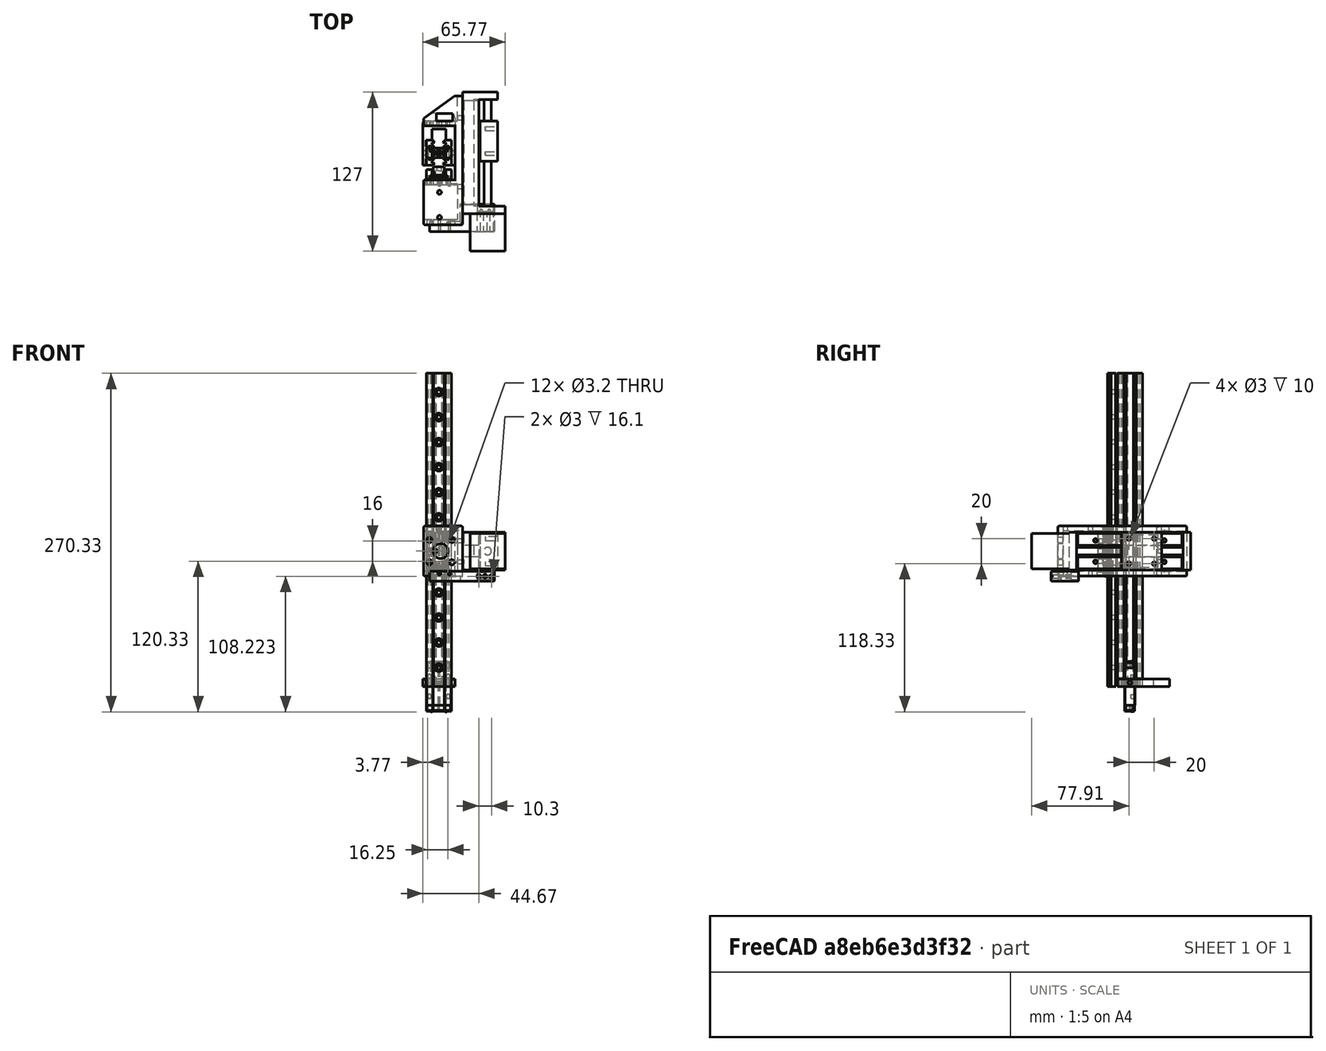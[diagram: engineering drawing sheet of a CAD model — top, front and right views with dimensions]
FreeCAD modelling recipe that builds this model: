
FCSTD DOCUMENT  (FreeCAD 1.0R39109 (Git))
Label: x_carriage
License: All rights reserved
LicenseURL: https://en.wikipedia.org/wiki/All_rights_reserved
objects: Sketcher::SketchObject×32, PartDesign::Pocket×19, PartDesign::Pad×17, Part::Feature×12, PartDesign::Mirrored×5, PartDesign::Body×4, PartDesign::LinearPattern×4, PartDesign::Fillet×4, PartDesign::MultiTransform×3, App::Part×2, Part::Mirroring×2, Part::Extrusion×1, Part::Fillet×1, Mesh::Feature×1
note: 228 computed .brp shape members not serialized (recipe doc carries the construction recipe); baked Part::Feature solids carry a one-line shape summary decoded from their .brp

FEATURE [Part::Feature] Part__Feature  label="MGN9-H"
  shape: bbox 20 x 8 x 29.9 mm, 47 faces (baked)
FEATURE [Part::Feature] Part__Feature001  label="MGN9-H001"
  shape: bbox 20 x 7.7 x 4.1 mm, 23 faces (baked)
FEATURE [Part::Feature] Part__Feature002  label="MGN9-H002"
  shape: bbox 2.603 x 2.603 x 1.283 mm, 15 faces (baked)
FEATURE [Part::Feature] Part__Feature003  label="MGN9-H003"
  shape: bbox 2.603 x 2.603 x 1.283 mm, 15 faces (baked)
FEATURE [Part::Feature] Part__Feature004  label="MGN9-H004"
  shape: bbox 20 x 7.7 x 0.9 mm, 57 faces (baked)
FEATURE [Part::Feature] Part__Feature005  label="MGN9-H005"
  shape: bbox 20 x 7.7 x 4.1 mm, 23 faces (baked)
FEATURE [Part::Feature] Part__Feature006  label="MGN9-H006"
  shape: bbox 20 x 7.7 x 0.9 mm, 57 faces (baked)
FEATURE [Part::Feature] Part__Feature007  label="MGN9-H007"
  shape: bbox 2.603 x 2.603 x 1.283 mm, 15 faces (baked)
FEATURE [Part::Feature] Part__Feature008  label="MGN9-H008"
  shape: bbox 2.603 x 2.603 x 1.283 mm, 15 faces (baked)
FEATURE [App::Part] MGN9_H  label="MGN9-H009"
  Group = -> [Part__Feature,Part__Feature001,Part__Feature002,Part__Feature003,Part__Feature004,Part__Feature005,Part__Feature006,Part__Feature007,Part__Feature008]
  Origin = -> Origin001
  Placement = pos=(0,17.3,108) rot=(0,0,1;0rad)
FEATURE [Part::Feature] Part__Feature009  label="MGN9"
  Placement = pos=(0,14.5,0) rot=(0,0,1;0rad)
  shape: bbox 9 x 6.5 x 250 mm, 130 faces (baked)
FEATURE [Sketcher::SketchObject] Sketch001
  ArcFitTolerance = 0
  FullyConstrained = false
  MakeInternals = false
  sketch-geometry (49):
    g0: Circle CenterX=0 CenterY=0 CenterZ=0 NormalX=0 NormalY=0 NormalZ=-1 AngleXU=0 Radius=2.1
    g1: LineSegment StartX=-2.84 StartY=3.90066 StartZ=0 EndX=-5.49934 EndY=6.56 EndZ=0
    g2: LineSegment StartX=-5.49934 StartY=6.56 StartZ=0 EndX=-5.49934 EndY=8.2 EndZ=0
    g3: LineSegment StartX=-5.49934 StartY=8.2 StartZ=0 EndX=-3.1 EndY=8.2 EndZ=0
    g4: LineSegment StartX=-3.1 StartY=8.2 StartZ=0 EndX=-4.9 EndY=10 EndZ=0
    g5: LineSegment StartX=-4.9 StartY=10 StartZ=0 EndX=-10 EndY=10 EndZ=0
    g6: LineSegment StartX=-10 StartY=10 StartZ=0 EndX=-10 EndY=4.9 EndZ=0
    g7: LineSegment StartX=-10 StartY=4.9 StartZ=0 EndX=-8.2 EndY=3.1 EndZ=0
    g8: LineSegment StartX=-8.2 StartY=3.1 StartZ=0 EndX=-8.2 EndY=5.49934 EndZ=0
    g9: LineSegment StartX=-8.2 StartY=5.49934 StartZ=0 EndX=-6.56 EndY=5.49934 EndZ=0
    g10: LineSegment StartX=-6.56 StartY=5.49934 StartZ=0 EndX=-3.90066 EndY=2.84 EndZ=0
    g11: LineSegment StartX=-3.90066 StartY=2.84 StartZ=0 EndX=-3.90066 EndY=-1.3e-15 EndZ=0
    g12: LineSegment StartX=-3.90066 StartY=-1.1e-15 StartZ=0 EndX=-3.90066 EndY=-2.84 EndZ=0
    g13: LineSegment StartX=-3.90066 StartY=-2.84 StartZ=0 EndX=-6.56 EndY=-5.49934 EndZ=0
    g14: LineSegment StartX=-6.56 StartY=-5.49934 StartZ=0 EndX=-8.2 EndY=-5.49934 EndZ=0
    g15: LineSegment StartX=-8.2 StartY=-5.49934 StartZ=0 EndX=-8.2 EndY=-3.1 EndZ=0
    g16: LineSegment StartX=-8.2 StartY=-3.1 StartZ=0 EndX=-10 EndY=-4.9 EndZ=0
    g17: LineSegment StartX=-10 StartY=-4.9 StartZ=0 EndX=-10 EndY=-10 EndZ=0
    g18: LineSegment StartX=-10 StartY=-10 StartZ=0 EndX=-4.9 EndY=-10 EndZ=0
    g19: LineSegment StartX=-4.9 StartY=-10 StartZ=0 EndX=-3.1 EndY=-8.2 EndZ=0
    g20: LineSegment StartX=-3.1 StartY=-8.2 StartZ=0 EndX=-5.49934 EndY=-8.2 EndZ=0
    g21: LineSegment StartX=-5.49934 StartY=-8.2 StartZ=0 EndX=-5.49934 EndY=-6.56 EndZ=0
    g22: LineSegment StartX=-5.49934 StartY=-6.56 StartZ=0 EndX=-2.84 EndY=-3.90066 EndZ=0
    g23: LineSegment StartX=-2.84 StartY=-3.90066 StartZ=0 EndX=-4e-16 EndY=-3.90066 EndZ=0
    g24: LineSegment StartX=-6e-16 StartY=-3.90066 StartZ=0 EndX=2.84 EndY=-3.90066 EndZ=0
    g25: LineSegment StartX=2.84 StartY=-3.90066 StartZ=0 EndX=5.49934 EndY=-6.56 EndZ=0
    g26: LineSegment StartX=5.49934 StartY=-6.56 StartZ=0 EndX=5.49934 EndY=-8.2 EndZ=0
    g27: LineSegment StartX=5.49934 StartY=-8.2 StartZ=0 EndX=3.1 EndY=-8.2 EndZ=0
    g28: LineSegment StartX=3.1 StartY=-8.2 StartZ=0 EndX=4.9 EndY=-10 EndZ=0
    g29: LineSegment StartX=4.9 StartY=-10 StartZ=0 EndX=10 EndY=-10 EndZ=0
    g30: LineSegment StartX=10 StartY=-10 StartZ=0 EndX=10 EndY=-4.9 EndZ=0
    g31: LineSegment StartX=10 StartY=-4.9 StartZ=0 EndX=8.2 EndY=-3.1 EndZ=0
    g32: LineSegment StartX=8.2 StartY=-3.1 StartZ=0 EndX=8.2 EndY=-5.49934 EndZ=0
    g33: LineSegment StartX=8.2 StartY=-5.49934 StartZ=0 EndX=6.56 EndY=-5.49934 EndZ=0
    g34: LineSegment StartX=6.56 StartY=-5.49934 StartZ=0 EndX=3.90066 EndY=-2.84 EndZ=0
    g35: LineSegment StartX=3.90066 StartY=-2.84 StartZ=0 EndX=3.90066 EndY=-1.3e-15 EndZ=0
    g36: LineSegment StartX=3.90066 StartY=-1.1e-15 StartZ=0 EndX=3.90066 EndY=2.84 EndZ=0
    g37: LineSegment StartX=3.90066 StartY=2.84 StartZ=0 EndX=6.56 EndY=5.49934 EndZ=0
    g38: LineSegment StartX=6.56 StartY=5.49934 StartZ=0 EndX=8.2 EndY=5.49934 EndZ=0
    g39: LineSegment StartX=8.2 StartY=5.49934 StartZ=0 EndX=8.2 EndY=3.1 EndZ=0
    g40: LineSegment StartX=8.2 StartY=3.1 StartZ=0 EndX=10 EndY=4.9 EndZ=0
    g41: LineSegment StartX=10 StartY=4.9 StartZ=0 EndX=10 EndY=10 EndZ=0
    g42: LineSegment StartX=10 StartY=10 StartZ=0 EndX=4.9 EndY=10 EndZ=0
    g43: LineSegment StartX=4.9 StartY=10 StartZ=0 EndX=3.1 EndY=8.2 EndZ=0
    g44: LineSegment StartX=3.1 StartY=8.2 StartZ=0 EndX=5.49934 EndY=8.2 EndZ=0
    g45: LineSegment StartX=5.49934 StartY=8.2 StartZ=0 EndX=5.49934 EndY=6.56 EndZ=0
    g46: LineSegment StartX=5.49934 StartY=6.56 StartZ=0 EndX=2.84 EndY=3.90066 EndZ=0
    g47: LineSegment StartX=2.84 StartY=3.90066 StartZ=0 EndX=0 EndY=3.90066 EndZ=0
    g48: LineSegment StartX=0 StartY=3.90066 StartZ=0 EndX=-2.84 EndY=3.90066 EndZ=0
FEATURE [Part::Extrusion] Extrude  label="2020"
  Base = -> Sketch001
  Dir = (0,0,1)
  DirMode = 2
  FaceMakerClass = Part::FaceMakerBullseye
  FaceMakerMode = 3
  LengthFwd = 250
  LengthRev = 0
  Solid = true
  Symmetric = false
FEATURE [Part::Fillet] Fillet  label="2020 V-slot"
  Base = -> Extrude
  EdgeLinks = -> Extrude [Edge14,Edge50,Edge86,Edge122]
  Edges = 4 edges r=1: [Edge14,Edge50,Edge86,Edge122]
FEATURE [Part::Mirroring] Part__Mirroring  label="MGN9-H009 (Mirror #1)"
  Base = (0,0,0)
  Normal = (0,1,0)
  Source = -> MGN9_H
FEATURE [Part::Mirroring] Part__Mirroring001  label="MGN9 (Mirror #2)"
  Base = (0,0,0)
  Normal = (0,1,0)
  Source = -> Part__Feature009
FEATURE [Sketcher::SketchObject] Sketch
  ArcFitTolerance = 1e-06
  AttachmentSupport = -> [YZ_Plane]
  FullyConstrained = true
  MakeInternals = false
  MapMode = 5
  Placement = pos=(0,0,0) rot=(0.57735,0.57735,0.57735;2.0944rad)
  sketch-geometry (5):
    g0: LineSegment StartX=-25.5 StartY=-20 StartZ=0 EndX=25.5 EndY=-20 EndZ=0
    g1: LineSegment StartX=25.5 StartY=-20 StartZ=0 EndX=25.5 EndY=20 EndZ=0
    g2: LineSegment StartX=25.5 StartY=20 StartZ=0 EndX=-25.5 EndY=20 EndZ=0
    g3: LineSegment StartX=-25.5 StartY=20 StartZ=0 EndX=-25.5 EndY=-20 EndZ=0
    g4: GeomPoint [constr] X=0 Y=0 Z=0
  constraints (12):
    c: Coincident(g0,g1)
    c: Coincident(g1,g2)
    c: Coincident(g2,g3)
    c: Coincident(g3,g0)
    c: Horizontal(g0)
    c: Horizontal(g2)
    c: Vertical(g1)
    c: Vertical(g3)
    c: Symmetric(g2,g0,g4)
    c: Distance(g1,g3) = 51
    c: Distance(g0,g2) = 40
    c: Coincident(g4,g-1)
FEATURE [PartDesign::Pad] Pad  label="carriageBase"
  Direction = (1,0,0)
  Length = 6
  Length2 = 10
  Placement = pos=(0,0,0) rot=(1,1,1;2.0944rad)
  Profile = -> Sketch
  ReferenceAxis = -> Sketch [N_Axis]
  Refine = true
  Suppressed = false
  Type = 0
FEATURE [Sketcher::SketchObject] Sketch002
  ArcFitTolerance = 1e-06
  AttachmentSupport = -> [Pad]
  ExternalGeometry = -> [Pad]
  FullyConstrained = true
  MakeInternals = false
  MapMode = 5
  Placement = pos=(0,0,0) rot=(0.57735,0.57735,-0.57735;4.18879rad)
  sketch-geometry (8):
    g0: LineSegment StartX=25.5 StartY=20 StartZ=0 EndX=21.5 EndY=20 EndZ=0
    g1: LineSegment StartX=21.5 StartY=20 StartZ=0 EndX=21.5 EndY=-20 EndZ=0
    g2: LineSegment StartX=21.5 StartY=-20 StartZ=0 EndX=25.5 EndY=-20 EndZ=0
    g3: LineSegment StartX=25.5 StartY=-20 StartZ=0 EndX=25.5 EndY=20 EndZ=0
    g4: LineSegment StartX=-25.5 StartY=20 StartZ=0 EndX=-25.5 EndY=-20 EndZ=0
    g5: LineSegment StartX=-25.5 StartY=-20 StartZ=0 EndX=-21.5 EndY=-20 EndZ=0
    g6: LineSegment StartX=-21.5 StartY=-20 StartZ=0 EndX=-21.5 EndY=20 EndZ=0
    g7: LineSegment StartX=-21.5 StartY=20 StartZ=0 EndX=-25.5 EndY=20 EndZ=0
  constraints (22):
    c: Coincident(g0,g1)
    c: Coincident(g1,g2)
    c: Coincident(g2,g3)
    c: Coincident(g3,g0)
    c: Horizontal(g0)
    c: Horizontal(g2)
    c: Vertical(g1)
    c: Vertical(g3)
    c: Distance(g1,g3) = 4
    c: Coincident(g0,g-3)
    c: PointOnObject(g1,g-4)
    c: Coincident(g4,g5)
    c: Coincident(g5,g6)
    c: Coincident(g6,g7)
    c: Coincident(g7,g4)
    c: Vertical(g4)
    c: Vertical(g6)
    c: Horizontal(g5)
    c: Horizontal(g7)
    c: Coincident(g4,g-3)
    c: PointOnObject(g5,g-4)
    c: Equal(g7,g0)
FEATURE [PartDesign::Pad] Pad001  label="carriageMountExtensions"
  BaseFeature = -> Pad
  Direction = (-1,0,0)
  Length = 25
  Length2 = 10
  Placement = pos=(0,0,0) rot=(1,1,1;2.0944rad)
  Profile = -> Sketch002
  ReferenceAxis = -> Sketch002 [N_Axis]
  Refine = true
  Suppressed = false
  Type = 0
FEATURE [Mesh::Feature] v2_belt_clamp_RL
  Placement = pos=(46,-56,87) rot=(0,1,0;3.14159rad)
FEATURE [Sketcher::SketchObject] Sketch003
  ArcFitTolerance = 1e-06
  AttachmentSupport = -> [XZ_Plane002]
  FullyConstrained = true
  MakeInternals = false
  MapMode = 5
  Placement = pos=(0,0,0) rot=(1,0,0;1.5708rad)
  sketch-geometry (5):
    g0: LineSegment StartX=-15 StartY=-48.5 StartZ=0 EndX=15 EndY=-48.5 EndZ=0
    g1: LineSegment StartX=15 StartY=-48.5 StartZ=0 EndX=15 EndY=48.5 EndZ=0
    g2: LineSegment StartX=15 StartY=48.5 StartZ=0 EndX=-15 EndY=48.5 EndZ=0
    g3: LineSegment StartX=-15 StartY=48.5 StartZ=0 EndX=-15 EndY=-48.5 EndZ=0
    g4: GeomPoint [constr] X=0 Y=0 Z=0
  constraints (12):
    c: Coincident(g0,g1)
    c: Coincident(g1,g2)
    c: Coincident(g2,g3)
    c: Coincident(g3,g0)
    c: Horizontal(g0)
    c: Horizontal(g2)
    c: Vertical(g1)
    c: Vertical(g3)
    c: Symmetric(g2,g0,g4)
    c: Distance(g1,g3) = 30
    c: Distance(g0,g2) = 97
    c: Coincident(g4,g-1)
FEATURE [PartDesign::Pad] Pad002  label="Base"
  Direction = (0,-1,2e-16)
  Length = 13
  Length2 = 10
  Placement = pos=(0,0,0) rot=(1,0,0;1.5708rad)
  Profile = -> Sketch003
  ReferenceAxis = -> Sketch003 [N_Axis]
  Refine = true
  Suppressed = false
  Type = 0
FEATURE [Sketcher::SketchObject] Sketch004
  ArcFitTolerance = 1e-06
  AttachmentSupport = -> [Pad002]
  ExternalGeometry = -> [Pad002]
  FullyConstrained = true
  MakeInternals = false
  MapMode = 5
  Placement = pos=(0,-13,0) rot=(1,0,0;1.5708rad)
  sketch-geometry (10):
    g0: LineSegment StartX=-15 StartY=-42.5 StartZ=0 EndX=-15 EndY=-48.5 EndZ=0
    g1: LineSegment StartX=-15 StartY=-48.5 StartZ=0 EndX=15 EndY=-48.5 EndZ=0
    g2: LineSegment StartX=15 StartY=-48.5 StartZ=0 EndX=15 EndY=-42.5 EndZ=0
    g3: LineSegment StartX=15 StartY=-42.5 StartZ=0 EndX=-15 EndY=-42.5 EndZ=0
    g4: GeomPoint [constr] X=0 Y=-45.5 Z=0
    g5: LineSegment StartX=-15 StartY=42.5 StartZ=0 EndX=15 EndY=42.5 EndZ=0
    g6: LineSegment StartX=15 StartY=42.5 StartZ=0 EndX=15 EndY=48.5 EndZ=0
    g7: LineSegment StartX=15 StartY=48.5 StartZ=0 EndX=-15 EndY=48.5 EndZ=0
    g8: LineSegment StartX=-15 StartY=48.5 StartZ=0 EndX=-15 EndY=42.5 EndZ=0
    g9: GeomPoint [constr] X=0 Y=45.5 Z=0
  constraints (24):
    c: Coincident(g0,g1)
    c: Coincident(g1,g2)
    c: Coincident(g2,g3)
    c: Coincident(g3,g0)
    c: Vertical(g0)
    c: Vertical(g2)
    c: Horizontal(g1)
    c: Horizontal(g3)
    c: Symmetric(g2,g0,g4)
    c: PointOnObject(g4,g-2)
    c: Coincident(g1,g-3)
    c: DistanceY(g1,g2) = 6
    c: Coincident(g5,g6)
    c: Coincident(g6,g7)
    c: Coincident(g7,g8)
    c: Coincident(g8,g5)
    c: Horizontal(g5)
    c: Horizontal(g7)
    c: Vertical(g6)
    c: Vertical(g8)
    c: Symmetric(g7,g5,g9)
    c: PointOnObject(g9,g-2)
    c: Coincident(g6,g-5)
    c: Equal(g6,g2)
FEATURE [PartDesign::Pad] Pad003  label="Flanges"
  BaseFeature = -> Pad002
  Direction = (0,-1,2e-16)
  Length = 15
  Length2 = 10
  Placement = pos=(0,0,0) rot=(1,0,0;1.5708rad)
  Profile = -> Sketch004
  ReferenceAxis = -> Sketch004 [N_Axis]
  Refine = true
  Suppressed = false
  Type = 0
FEATURE [PartDesign::Pad] Pad004  label="FlangeExtension"
  BaseFeature = -> Pad003
  Direction = (0,-1,0)
  Length = 6
  Length2 = 10
  Placement = pos=(0,0,0) rot=(1,0,0;1.5708rad)
  Profile = -> Pad003 [Face5]
  Refine = true
  Suppressed = false
  Type = 0
FEATURE [Sketcher::SketchObject] Sketch005
  ArcFitTolerance = 1e-06
  AttachmentSupport = -> [Pad004]
  ExternalGeometry = -> [Pad004]
  FullyConstrained = true
  MakeInternals = false
  MapMode = 5
  Placement = pos=(0,2.09e-14,48.5) rot=(0,0,1;3.14159rad)
  sketch-geometry (5):
    g0: LineSegment StartX=-14 StartY=6 StartZ=0 EndX=14 EndY=6 EndZ=0
    g1: LineSegment StartX=14 StartY=6 StartZ=0 EndX=14 EndY=34 EndZ=0
    g2: LineSegment StartX=14 StartY=34 StartZ=0 EndX=-14 EndY=34 EndZ=0
    g3: LineSegment StartX=-14 StartY=34 StartZ=0 EndX=-14 EndY=6 EndZ=0
    g4: GeomPoint [constr] X=0 Y=20 Z=0
  constraints (13):
    c: Coincident(g0,g1)
    c: Coincident(g1,g2)
    c: Coincident(g2,g3)
    c: Coincident(g3,g0)
    c: Horizontal(g0)
    c: Horizontal(g2)
    c: Vertical(g1)
    c: Vertical(g3)
    c: Symmetric(g2,g0,g4)
    c: Distance(g1,g3) = 28
    c: PointOnObject(g2,g-3)
    c: PointOnObject(g4,g-2)
    c: Equal(g1,g2)
FEATURE [PartDesign::Pad] Pad005  label="Stepper"
  BaseFeature = -> Pad004
  Direction = (0,0,1)
  Length = 30
  Length2 = 10
  Placement = pos=(0,0,0) rot=(1,0,0;1.5708rad)
  Profile = -> Sketch005
  ReferenceAxis = -> Sketch005 [N_Axis]
  Refine = true
  Suppressed = false
  Type = 0
FEATURE [Sketcher::SketchObject] Sketch006
  ArcFitTolerance = 1e-06
  AttachmentOffset = pos=(0,10,0) rot=(0,0,1;0rad)
  AttachmentSupport = -> [Pad005]
  FullyConstrained = false
  MakeInternals = false
  MapMode = 5
  Placement = pos=(0,-13,10) rot=(1,0,0;1.5708rad)
  sketch-geometry (5):
    g0: LineSegment StartX=-13 StartY=-32.4103 StartZ=0 EndX=13 EndY=-32.4103 EndZ=0
    g1: LineSegment StartX=13 StartY=-32.4103 StartZ=0 EndX=13 EndY=-6.41029 EndZ=0
    g2: LineSegment StartX=13 StartY=-6.41029 StartZ=0 EndX=-13 EndY=-6.41029 EndZ=0
    g3: LineSegment StartX=-13 StartY=-6.41029 StartZ=0 EndX=-13 EndY=-32.4103 EndZ=0
    g4: GeomPoint [constr] X=0 Y=-19.4103 Z=0
  constraints (12):
    c: Coincident(g0,g1)
    c: Coincident(g1,g2)
    c: Coincident(g2,g3)
    c: Coincident(g3,g0)
    c: Horizontal(g0)
    c: Horizontal(g2)
    c: Vertical(g1)
    c: Vertical(g3)
    c: Symmetric(g2,g0,g4)
    c: Distance(g1,g3) = 26
    c: Distance(g0,g2) = 26
    c: DistanceX(g-1,g4) = 0
FEATURE [PartDesign::Pad] Pad006  label="TableBase"
  BaseFeature = -> Pad005
  Direction = (0,-1,2e-16)
  Length = 1
  Length2 = 10
  Placement = pos=(0,0,0) rot=(1,0,0;1.5708rad)
  Profile = -> Sketch006
  ReferenceAxis = -> Sketch006 [N_Axis]
  Refine = true
  Suppressed = false
  Type = 0
FEATURE [Sketcher::SketchObject] Sketch007
  ArcFitTolerance = 1e-06
  AttachmentSupport = -> [Pad006]
  ExternalGeometry = -> [Pad006]
  FullyConstrained = true
  MakeInternals = false
  MapMode = 5
  Placement = pos=(0,-14,0) rot=(1,0,0;1.5708rad)
  sketch-geometry (8):
    g0: LineSegment StartX=-15 StartY=-25.4103 StartZ=0 EndX=15 EndY=-25.4103 EndZ=0
    g1: LineSegment StartX=15 StartY=-25.4103 StartZ=0 EndX=15 EndY=6.58971 EndZ=0
    g2: LineSegment StartX=15 StartY=6.58971 StartZ=0 EndX=-15 EndY=6.58971 EndZ=0
    g3: LineSegment StartX=-15 StartY=6.58971 StartZ=0 EndX=-15 EndY=-25.4103 EndZ=0
    g4: GeomPoint [constr] X=0 Y=-9.41029 Z=0
    g5: GeomPoint [constr] X=13 Y=-9.41029 Z=0
    g6: GeomPoint [constr] X=-3e-16 Y=3.58971 Z=0
    g7: GeomPoint [constr] X=0 Y=-9.41029 Z=0
  constraints (16):
    c: Coincident(g0,g1)
    c: Coincident(g1,g2)
    c: Coincident(g2,g3)
    c: Coincident(g3,g0)
    c: Horizontal(g0)
    c: Horizontal(g2)
    c: Vertical(g1)
    c: Vertical(g3)
    c: Symmetric(g2,g0,g4)
    c: Distance(g1,g3) = 30
    c: Distance(g0,g2) = 32
    c: DistanceX(g-1,g4) = 0
    c: Symmetric(g-4,g-4,g5)
    c: Symmetric(g-3,g-3,g6)
    c: DistanceY(g5,g7) = 0
    c: Coincident(g4,g7)
FEATURE [PartDesign::Pad] Pad007  label="TableMount"
  BaseFeature = -> Pad006
  Direction = (0,-1,2e-16)
  Length = 14
  Length2 = 10
  Placement = pos=(0,0,0) rot=(1,0,0;1.5708rad)
  Profile = -> Sketch007
  ReferenceAxis = -> Sketch007 [N_Axis]
  Refine = true
  Suppressed = false
  Type = 0
FEATURE [Sketcher::SketchObject] Sketch008
  ArcFitTolerance = 1e-06
  AttachmentSupport = -> [Pad007]
  ExternalGeometry = -> [Pad007]
  FullyConstrained = true
  MakeInternals = false
  MapMode = 5
  Placement = pos=(0,-28,0) rot=(1,0,0;1.5708rad)
  sketch-geometry (4):
    g0: Circle CenterX=-10 CenterY=0.589709 CenterZ=0 NormalX=0 NormalY=0 NormalZ=1 AngleXU=0 Radius=1.5
    g1: Circle CenterX=10 CenterY=0.589709 CenterZ=0 NormalX=0 NormalY=0 NormalZ=1 AngleXU=0 Radius=1.5
    g2: Circle CenterX=10 CenterY=-19.4103 CenterZ=0 NormalX=0 NormalY=0 NormalZ=1 AngleXU=0 Radius=1.5
    g3: Circle CenterX=-10 CenterY=-19.4103 CenterZ=0 NormalX=0 NormalY=0 NormalZ=1 AngleXU=0 Radius=1.5
  constraints (12):
    c: Diameter(g0) = 3
    c: Equal(g1,g0)
    c: Equal(g0,g3)
    c: Equal(g3,g2)
    c: DistanceY(g0,g-5) = 6
    c: DistanceX(g-5,g0) = 5
    c: DistanceY(g1,g0) = 0
    c: DistanceX(g3,g0) = 0
    c: DistanceY(g3,g2) = 0
    c: DistanceX(g2,g1) = 0
    c: DistanceY(g3,g0) = 20
    c: DistanceX(g0,g1) = 20
FEATURE [PartDesign::Pocket] Pocket  label="TableMountingHoles"
  BaseFeature = -> Pad007
  Direction = (0,1,-2e-16)
  Length = 10
  Length2 = 5
  Placement = pos=(0,0,0) rot=(1,0,0;1.5708rad)
  Profile = -> Sketch008
  ReferenceAxis = -> Sketch008 [N_Axis]
  Refine = true
  Suppressed = false
  Type = 0
FEATURE [Sketcher::SketchObject] Sketch009
  ArcFitTolerance = 1e-06
  AttachmentSupport = -> [Pocket]
  ExternalGeometry = -> [Pocket]
  FullyConstrained = true
  MakeInternals = false
  MapMode = 5
  Placement = pos=(0,2.55e-14,42.5) rot=(1,0,0;3.14159rad)
  sketch-geometry (1):
    g0: Circle CenterX=0 CenterY=20 CenterZ=0 NormalX=0 NormalY=0 NormalZ=1 AngleXU=0 Radius=3
  constraints (3):
    c: PointOnObject(g0,g-2)
    c: DistanceY(g0,g-3) = 14
    c: Diameter(g0) = 6
FEATURE [PartDesign::Pad] Pad008  label="BallScrew"
  BaseFeature = -> Pocket
  Direction = (0,0,-1)
  Length = 85
  Length2 = 10
  Placement = pos=(0,0,0) rot=(1,0,0;1.5708rad)
  Profile = -> Sketch009
  ReferenceAxis = -> Sketch009 [N_Axis]
  Refine = true
  Suppressed = false
  Type = 0
FEATURE [Sketcher::SketchObject] Sketch010
  ArcFitTolerance = 1e-06
  AttachmentSupport = -> [Pad008]
  FullyConstrained = true
  MakeInternals = false
  MapMode = 5
  Placement = pos=(0,-13,0) rot=(1,0,0;1.5708rad)
  sketch-geometry (5):
    g0: LineSegment StartX=-4.5 StartY=-42.5 StartZ=0 EndX=4.5 EndY=-42.5 EndZ=0
    g1: LineSegment StartX=4.5 StartY=-42.5 StartZ=0 EndX=4.5 EndY=42.5 EndZ=0
    g2: LineSegment StartX=4.5 StartY=42.5 StartZ=0 EndX=-4.5 EndY=42.5 EndZ=0
    g3: LineSegment StartX=-4.5 StartY=42.5 StartZ=0 EndX=-4.5 EndY=-42.5 EndZ=0
    g4: GeomPoint [constr] X=0 Y=0 Z=0
  constraints (12):
    c: Coincident(g0,g1)
    c: Coincident(g1,g2)
    c: Coincident(g2,g3)
    c: Coincident(g3,g0)
    c: Horizontal(g0)
    c: Horizontal(g2)
    c: Vertical(g1)
    c: Vertical(g3)
    c: Symmetric(g2,g0,g4)
    c: Distance(g1,g3) = 9
    c: Distance(g0,g2) = 85
    c: Coincident(g4,g-1)
FEATURE [PartDesign::Pocket] Pocket001  label="Slide"
  BaseFeature = -> Pad008
  Direction = (0,1,-2e-16)
  Length = 4
  Length2 = 5
  Placement = pos=(0,0,0) rot=(1,0,0;1.5708rad)
  Profile = -> Sketch010
  ReferenceAxis = -> Sketch010 [N_Axis]
  Refine = true
  Suppressed = false
  Type = 0
FEATURE [Sketcher::SketchObject] Sketch011
  ArcFitTolerance = 1e-06
  AttachmentSupport = -> [Pocket001]
  ExternalGeometry = -> [Pocket001]
  FullyConstrained = true
  MakeInternals = false
  MapMode = 5
  Placement = pos=(0,0,0) rot=(-1,0,0;1.5708rad)
  sketch-geometry (4):
    g0: Circle CenterX=-8.5 CenterY=27.5 CenterZ=0 NormalX=0 NormalY=0 NormalZ=1 AngleXU=0 Radius=1.5
    g1: Circle CenterX=8.5 CenterY=27.5 CenterZ=0 NormalX=0 NormalY=0 NormalZ=1 AngleXU=0 Radius=1.5
    g2: Circle CenterX=8.5 CenterY=-27.5 CenterZ=0 NormalX=0 NormalY=0 NormalZ=1 AngleXU=0 Radius=1.5
    g3: Circle CenterX=-8.5 CenterY=-27.5 CenterZ=0 NormalX=0 NormalY=0 NormalZ=1 AngleXU=0 Radius=1.5
  constraints (10):
    c: Diameter(g0) = 3
    c: Equal(g3,g2)
    c: Equal(g2,g1)
    c: Equal(g1,g0)
    c: DistanceY(g0,g-3) = 21
    c: DistanceX(g0,g1) = 17
    c: Symmetric(g1,g0,g-2)
    c: DistanceX(g3,g2) = 17
    c: Symmetric(g3,g2,g-2)
    c: DistanceY(g-4,g3) = 21
FEATURE [PartDesign::Pocket] Pocket002  label="MountingHoles"
  BaseFeature = -> Pocket001
  Direction = (0,-1,-2e-16)
  Length = 14
  Length2 = 5
  Placement = pos=(0,0,0) rot=(1,0,0;1.5708rad)
  Profile = -> Sketch011
  ReferenceAxis = -> Sketch011 [N_Axis]
  Refine = true
  Suppressed = false
  Type = 0
FEATURE [Sketcher::SketchObject] Sketch028
  ArcFitTolerance = 1e-06
  AttachmentSupport = -> [Pocket002]
  ExternalGeometry = -> [Pocket002]
  FullyConstrained = true
  MakeInternals = false
  MapMode = 5
  Placement = pos=(0,-13,0) rot=(1,0,0;1.5708rad)
  sketch-geometry (5):
    g0: LineSegment StartX=-4.5 StartY=-41.5 StartZ=0 EndX=-4.5 EndY=41.5 EndZ=0
    g1: LineSegment StartX=-4.5 StartY=41.5 StartZ=0 EndX=-14 EndY=41.5 EndZ=0
    g2: LineSegment StartX=-14 StartY=41.5 StartZ=0 EndX=-14 EndY=-41.5 EndZ=0
    g3: LineSegment StartX=-14 StartY=-41.5 StartZ=0 EndX=-4.5 EndY=-41.5 EndZ=0
    g4: GeomPoint [constr] X=-9.25 Y=0 Z=0
  constraints (13):
    c: Coincident(g0,g1)
    c: Coincident(g1,g2)
    c: Coincident(g2,g3)
    c: Coincident(g3,g0)
    c: Vertical(g0)
    c: Vertical(g2)
    c: Horizontal(g1)
    c: Horizontal(g3)
    c: Symmetric(g2,g0,g4)
    c: PointOnObject(g4,g-1)
    c: DistanceY(g1,g-4) = 1
    c: DistanceX(g-4,g1) = 1
    c: DistanceX(g0,g-3) = 0
FEATURE [PartDesign::Pocket] Pocket007  label="SlideInsetLeft"
  BaseFeature = -> Pocket002
  Direction = (0,1,-2e-16)
  Length = 12
  Length2 = 5
  Placement = pos=(0,0,0) rot=(1,0,0;1.5708rad)
  Profile = -> Sketch028
  ReferenceAxis = -> Sketch028 [N_Axis]
  Refine = true
  Suppressed = false
  Type = 0
FEATURE [Sketcher::SketchObject] Sketch029
  ArcFitTolerance = 1e-06
  AttachmentSupport = -> [Pocket007]
  ExternalGeometry = -> [Pocket007]
  FullyConstrained = true
  MakeInternals = false
  MapMode = 5
  Placement = pos=(0,-13,0) rot=(1,0,0;1.5708rad)
  sketch-geometry (5):
    g0: LineSegment StartX=4.5 StartY=-41.5 StartZ=0 EndX=14 EndY=-41.5 EndZ=0
    g1: LineSegment StartX=14 StartY=-41.5 StartZ=0 EndX=14 EndY=41.5 EndZ=0
    g2: LineSegment StartX=14 StartY=41.5 StartZ=0 EndX=4.5 EndY=41.5 EndZ=0
    g3: LineSegment StartX=4.5 StartY=41.5 StartZ=0 EndX=4.5 EndY=-41.5 EndZ=0
    g4: GeomPoint [constr] X=9.25 Y=0 Z=0
  constraints (13):
    c: Coincident(g0,g1)
    c: Coincident(g1,g2)
    c: Coincident(g2,g3)
    c: Coincident(g3,g0)
    c: Horizontal(g0)
    c: Horizontal(g2)
    c: Vertical(g1)
    c: Vertical(g3)
    c: Symmetric(g2,g0,g4)
    c: PointOnObject(g4,g-1)
    c: DistanceY(g1,g-3) = 1
    c: DistanceX(g1,g-3) = 1
    c: DistanceX(g-4,g2) = 0
FEATURE [PartDesign::Pocket] Pocket008  label="SlideInsetRight"
  BaseFeature = -> Pocket007
  Direction = (0,1,-2e-16)
  Length = 12
  Length2 = 5
  Placement = pos=(0,0,0) rot=(1,0,0;1.5708rad)
  Profile = -> Sketch029
  ReferenceAxis = -> Sketch029 [N_Axis]
  Refine = true
  Suppressed = false
  Type = 0
FEATURE [PartDesign::Body] Body001  label="SlideTable50mm"
  AllowCompound = false
  Group = -> [Sketch003,Pad002,Sketch004,Pad003,Pad004,Sketch005,Pad005,Sketch006,Pad006,Sketch007,Pad007,Sketch008,Pocket,Sketch009,Pad008,Sketch010,Pocket001,Sketch011,Pocket002,Sketch028,Pocket007,Sketch029,Pocket008]
  Origin = -> Origin002
  Placement = pos=(19,-6.4e-15,108) rot=(0.57735,-0.57735,0.57735;2.0944rad)
  Tip = -> Pocket008
FEATURE [Sketcher::SketchObject] Sketch030
  ArcFitTolerance = 1e-06
  AttachmentSupport = -> [Pad001]
  ExternalGeometry = -> [Pad001]
  FullyConstrained = true
  MakeInternals = false
  MapMode = 5
  Placement = pos=(7.7e-15,25.5,0) rot=(0.57735,0.57735,0.57735;4.18879rad)
  sketch-geometry (8):
    g0: LineSegment StartX=-16 StartY=-25 StartZ=0 EndX=-20 EndY=-25 EndZ=0
    g1: LineSegment StartX=-20 StartY=-25 StartZ=0 EndX=-20 EndY=6 EndZ=0
    g2: LineSegment StartX=-20 StartY=6 StartZ=0 EndX=20 EndY=6 EndZ=0
    g3: LineSegment StartX=20 StartY=6 StartZ=0 EndX=20 EndY=-25 EndZ=0
    g4: LineSegment StartX=20 StartY=-25 StartZ=0 EndX=16 EndY=-25 EndZ=0
    g5: LineSegment StartX=16 StartY=-25 StartZ=0 EndX=16 EndY=2 EndZ=0
    g6: LineSegment StartX=16 StartY=2 StartZ=0 EndX=-16 EndY=2 EndZ=0
    g7: LineSegment StartX=-16 StartY=2 StartZ=0 EndX=-16 EndY=-25 EndZ=0
  constraints (20):
    c: PointOnObject(g0,g-6)
    c: Coincident(g0,g-6)
    c: Coincident(g0,g1)
    c: Coincident(g1,g-4)
    c: Coincident(g1,g2)
    c: Coincident(g2,g-5)
    c: Coincident(g2,g3)
    c: Coincident(g3,g-6)
    c: Coincident(g3,g4)
    c: PointOnObject(g4,g-6)
    c: Coincident(g4,g5)
    c: Vertical(g5)
    c: Coincident(g5,g6)
    c: Horizontal(g6)
    c: Coincident(g6,g7)
    c: Coincident(g7,g0)
    c: Vertical(g7)
    c: Equal(g0,g4)
    c: DistanceX(g4,g4) = 4
    c: DistanceY(g5,g2) = 4
FEATURE [PartDesign::Pad] Pad009  label="slideMountLower"
  BaseFeature = -> Pad001
  Direction = (0,1,0)
  Length = 20
  Length2 = 10
  Placement = pos=(0,0,0) rot=(1,1,1;2.0944rad)
  Profile = -> Sketch030
  ReferenceAxis = -> Sketch030 [N_Axis]
  Refine = true
  Suppressed = false
  Type = 0
FEATURE [Sketcher::SketchObject] Sketch031
  ArcFitTolerance = 1e-06
  AttachmentSupport = -> [Pad009]
  ExternalGeometry = -> [Pad009]
  FullyConstrained = true
  MakeInternals = false
  MapMode = 5
  Placement = pos=(0,-1.14e-14,-20) rot=(0.707107,0.707107,0;3.14159rad)
  sketch-geometry (7):
    g0: LineSegment StartX=27.5 StartY=-25 StartZ=0 EndX=45.5 EndY=-2.13e-14 EndZ=0
    g1: LineSegment StartX=45.5 StartY=-2.21e-14 StartZ=0 EndX=45.5 EndY=-25 EndZ=0
    g2: LineSegment StartX=45.5 StartY=-25 StartZ=0 EndX=27.5 EndY=-25 EndZ=0
    g3: LineSegment StartX=25.5 StartY=-2 StartZ=0 EndX=25.5 EndY=-14.9 EndZ=0
    g4: LineSegment StartX=25.5 StartY=-14.9 StartZ=0 EndX=31.4 EndY=-14.9 EndZ=0
    g5: LineSegment StartX=31.4 StartY=-14.9 StartZ=0 EndX=31.4 EndY=-2 EndZ=0
    g6: LineSegment StartX=31.4 StartY=-2 StartZ=0 EndX=25.5 EndY=-2 EndZ=0
  constraints (20):
    c: PointOnObject(g0,g-4)
    c: PointOnObject(g0,g-3)
    c: Coincident(g0,g1)
    c: Coincident(g1,g-4)
    c: Coincident(g1,g2)
    c: Coincident(g2,g0)
    c: DistanceX(g-5,g0) = 2
    c: DistanceY(g0,g-6) = 2
    c: Coincident(g3,g4)
    c: Coincident(g4,g5)
    c: Coincident(g5,g6)
    c: Coincident(g6,g3)
    c: Vertical(g3)
    c: Vertical(g5)
    c: Horizontal(g4)
    c: Horizontal(g6)
    c: Distance(g3,g5) = 5.9
    c: Distance(g4,g6) = 12.9
    c: DistanceY(g5,g-3) = 8
    c: DistanceX(g-5,g3) = 0
FEATURE [PartDesign::Pocket] Pocket009  label="slideMountlowerTriangleCutout"
  BaseFeature = -> Pad009
  Direction = (0,0,1)
  Length = 40
  Length2 = 5
  Placement = pos=(0,0,0) rot=(1,1,1;2.0944rad)
  Profile = -> Sketch031
  ReferenceAxis = -> Sketch031 [N_Axis]
  Refine = true
  Suppressed = false
  Type = 0
FEATURE [PartDesign::Mirrored] Mirrored  label="slideMountUpper"
  BaseFeature = -> Pocket009
  MirrorPlane = -> XZ_Plane
  Originals = -> [Pad009]
  Placement = pos=(0,0,0) rot=(1,1,1;2.0944rad)
  Refine = true
  Suppressed = false
  TransformMode = 0
FEATURE [PartDesign::Pad] Pad010  label="carriageBeltClipExtension"
  BaseFeature = -> Mirrored
  Direction = (-3e-16,-1,-1e-16)
  Length = 12
  Length2 = 10
  Placement = pos=(0,0,0) rot=(1,1,1;2.0944rad)
  Profile = -> Mirrored [Face21]
  Refine = true
  Suppressed = false
  Type = 0
FEATURE [Sketcher::SketchObject] Sketch032
  ArcFitTolerance = 1e-06
  AttachmentSupport = -> [Pad010]
  ExternalGeometry = -> [Pad010]
  FullyConstrained = true
  MakeInternals = false
  MapMode = 5
  Placement = pos=(0,-25.5,0) rot=(0.57735,0.57735,-0.57735;2.0944rad)
  sketch-geometry (19):
    g0: Circle CenterX=-8 CenterY=-5.75 CenterZ=0 NormalX=0 NormalY=0 NormalZ=1 AngleXU=0 Radius=1.6
    g1: Circle CenterX=8 CenterY=-5.75 CenterZ=0 NormalX=0 NormalY=0 NormalZ=1 AngleXU=0 Radius=1.6
    g2: Circle CenterX=8 CenterY=-20.75 CenterZ=0 NormalX=0 NormalY=0 NormalZ=1 AngleXU=0 Radius=1.6
    g3: Circle CenterX=-8 CenterY=-20.75 CenterZ=0 NormalX=0 NormalY=0 NormalZ=1 AngleXU=0 Radius=1.6
    g4: Circle CenterX=-14.9 CenterY=-5.2 CenterZ=0 NormalX=0 NormalY=0 NormalZ=1 AngleXU=0 Radius=1.025
    g5: Circle CenterX=-14.9 CenterY=-11.7 CenterZ=0 NormalX=0 NormalY=0 NormalZ=1 AngleXU=0 Radius=1.025
    g6: GeomPoint [constr] X=-20 Y=-5.61982 Z=0
    g7: GeomPoint X=-20 Y=-5.61982 Z=0
    g8: LineSegment [constr] StartX=-14.9 StartY=-5.2 StartZ=0 EndX=-14.9 EndY=-11.7 EndZ=0
    g9: GeomPoint [constr] X=-14.9 Y=-8.45 Z=0
    g10: LineSegment [constr] StartX=-8 StartY=-5.75 StartZ=0 EndX=-8 EndY=-20.75 EndZ=0
    g11: GeomPoint [constr] X=-8 Y=-13.25 Z=0
    g12: Circle CenterX=14.9 CenterY=-5.2 CenterZ=0 NormalX=0 NormalY=0 NormalZ=1 AngleXU=0 Radius=1.025
    g13: Circle CenterX=14.9 CenterY=-11.7 CenterZ=0 NormalX=0 NormalY=0 NormalZ=1 AngleXU=0 Radius=1.025
    g14: LineSegment [constr] StartX=14.9 StartY=-5.2 StartZ=0 EndX=14.9 EndY=-11.7 EndZ=0
    g15: GeomPoint [constr] X=14.9 Y=-8.45 Z=0
    g16: GeomPoint [constr] X=20 Y=-5.61982 Z=0
    g17: Circle CenterX=0 CenterY=-16 CenterZ=0 NormalX=0 NormalY=0 NormalZ=1 AngleXU=0 Radius=1.6
    g18: Circle CenterX=0 CenterY=-22 CenterZ=0 NormalX=0 NormalY=0 NormalZ=1 AngleXU=0 Radius=1.6
  constraints (41):
    c: Equal(g0,g1)
    c: Equal(g1,g2)
    c: Equal(g2,g3)
    c: Diameter(g0) = 3.2
    c: DistanceX(g0,g1) = 16
    c: DistanceY(g2,g1) = 15
    c: DistanceY(g2,g3) = 0
    c: DistanceX(g0,g3) = 0
    c: DistanceX(g2,g1) = 0
    c: Symmetric(g0,g1,g-2)
    c: DistanceY(g1,g-1) = 5.75
    c: Diameter(g4) = 2.05
    c: Diameter(g5) = 2.05
    c: DistanceY(g5,g4) = 6.5
    c: Symmetric(g-4,g-4,g6)
    c: Coincident(g7,g6)
    c: DistanceX(g6,g4) = 5.1
    c: DistanceX(g4,g5) = 0
    c: Coincident(g8,g4)
    c: Coincident(g8,g5)
    c: Symmetric(g8,g8,g9)
    c: Coincident(g10,g0)
    c: Coincident(g10,g3)
    c: Symmetric(g10,g10,g11)
    c: Diameter(g12) = 2.05
    c: Diameter(g13) = 2.05
    c: DistanceY(g13,g12) = 6.5
    c: DistanceX(g12,g13) = 0
    c: Coincident(g14,g12)
    c: Coincident(g14,g13)
    c: Symmetric(g14,g14,g15)
    c: DistanceY(g4,g12) = 0
    c: Symmetric(g-3,g-3,g16)
    c: DistanceX(g12,g16) = 5.1
    c: DistanceY(g4,g-5) = 11.2
    c: Diameter(g17) = 3.2
    c: PointOnObject(g17,g-2)
    c: Diameter(g18) = 3.2
    c: PointOnObject(g18,g-2)
    c: DistanceY(g18,g17) = 6
    c: DistanceY(g-6,g18) = 3
FEATURE [PartDesign::Pocket] Pocket010  label="carriageMountHoles"
  BaseFeature = -> Pad010
  Direction = (1e-16,1,-1e-15)
  Length = 5
  Length2 = 5
  Placement = pos=(0,0,0) rot=(1,1,1;2.0944rad)
  Profile = -> Sketch032
  ReferenceAxis = -> Sketch032 [N_Axis]
  Refine = true
  Suppressed = false
  Type = 0
FEATURE [PartDesign::Mirrored] Mirrored001  label="carriageMountHolesLower"
  BaseFeature = -> Pocket010
  MirrorPlane = -> XZ_Plane
  Originals = -> [Pocket010]
  Placement = pos=(0,0,0) rot=(1,1,1;2.0944rad)
  Refine = true
  Suppressed = false
  TransformMode = 0
FEATURE [Sketcher::SketchObject] Sketch033
  ArcFitTolerance = 1e-06
  AttachmentSupport = -> [Mirrored001]
  ExternalGeometry = -> [Mirrored001]
  FullyConstrained = true
  MakeInternals = false
  MapMode = 5
  Placement = pos=(6,0,7.4e-15) rot=(0.57735,0.57735,0.57735;2.0944rad)
  sketch-geometry (4):
    g0: Circle CenterX=-27 CenterY=8.5 CenterZ=0 NormalX=0 NormalY=0 NormalZ=1 AngleXU=0 Radius=1.6
    g1: Circle CenterX=28 CenterY=8.5 CenterZ=0 NormalX=0 NormalY=0 NormalZ=1 AngleXU=0 Radius=1.6
    g2: Circle CenterX=28 CenterY=-8.5 CenterZ=0 NormalX=0 NormalY=0 NormalZ=1 AngleXU=0 Radius=1.6
    g3: Circle CenterX=-27 CenterY=-8.5 CenterZ=0 NormalX=0 NormalY=0 NormalZ=1 AngleXU=0 Radius=1.6
  constraints (11):
    c: Equal(g0,g2)
    c: Equal(g2,g3)
    c: Equal(g3,g1)
    c: Diameter(g0) = 3.2
    c: DistanceY(g1,g0) = 0
    c: DistanceY(g2,g3) = 0
    c: DistanceX(g2,g1) = 0
    c: DistanceY(g3,g0) = 17
    c: Symmetric(g0,g3,g-1)
    c: DistanceX(g0,g1) = 55
    c: DistanceX(g1,g-3) = 17.5
FEATURE [PartDesign::Pocket] Pocket011  label="slideTableMountHoles"
  BaseFeature = -> Mirrored001
  Direction = (-1,-1e-16,-1.4e-15)
  Length = 5
  Length2 = 5
  Placement = pos=(0,0,0) rot=(1,1,1;2.0944rad)
  Profile = -> Sketch033
  ReferenceAxis = -> Sketch033 [N_Axis]
  Refine = true
  Suppressed = false
  Type = 0
FEATURE [Part::Feature] Part__Feature010  label="M3 Nyloc Nut"
  shape: bbox 6.171 x 6.065 x 4.061 mm, 62 faces (baked)
FEATURE [Part::Feature] Part__Feature011  label="M3 Nyloc Nut001"
  shape: bbox 3.3 x 3.3 x 0.9 mm, 6 faces (baked)
FEATURE [App::Part] M3_Nyloc_Nut  label="M3 Nyloc Nut002"
  Group = -> [Part__Feature010,Part__Feature011]
  Origin = -> Origin003
  Placement = pos=(14.94,-27.63,99.27) rot=(0,1,0;4.71239rad)
FEATURE [Sketcher::SketchObject] Sketch034
  ArcFitTolerance = 1e-06
  AttachmentSupport = -> [Pocket011]
  FullyConstrained = true
  MakeInternals = false
  MapMode = 5
  Placement = pos=(2,0,1.5e-15) rot=(0.57735,0.57735,-0.57735;4.18879rad)
  sketch-geometry (7):
    g0: LineSegment StartX=-27.5 StartY=-5.42 StartZ=0 EndX=-30.1674 EndY=-6.96 EndZ=0
    g1: LineSegment StartX=-30.1674 StartY=-6.96 StartZ=0 EndX=-30.1674 EndY=-10.04 EndZ=0
    g2: LineSegment StartX=-30.1674 StartY=-10.04 StartZ=0 EndX=-27.5 EndY=-11.58 EndZ=0
    g3: LineSegment StartX=-27.5 StartY=-11.58 StartZ=0 EndX=-24.8326 EndY=-10.04 EndZ=0
    g4: LineSegment StartX=-24.8326 StartY=-10.04 StartZ=0 EndX=-24.8326 EndY=-6.96 EndZ=0
    g5: LineSegment StartX=-24.8326 StartY=-6.96 StartZ=0 EndX=-27.5 EndY=-5.42 EndZ=0
    g6: Circle [constr] CenterX=-27.5 CenterY=-8.5 CenterZ=0 NormalX=0 NormalY=0 NormalZ=1 AngleXU=0 Radius=3.08
  constraints (16):
    c: Coincident(g0,g1)
    c: Coincident(g1,g2)
    c: Coincident(g2,g3)
    c: Coincident(g3,g4)
    c: Coincident(g4,g5)
    c: Coincident(g5,g0)
    c: Equal(g0, g1-g5) x5
    c: PointOnObject(g0,g6)
    c: PointOnObject(g1,g6)
    c: PointOnObject(g2,g6)
    c: PointOnObject(g3,g6)
    c: PointOnObject(g4,g6)
    c: PointOnObject(g5,g6)
    c: Radius(g6) = 3.08
    c: Coincident(g6,g-3)
    c: Perpendicular(g-1,g1)
FEATURE [PartDesign::Pocket] Pocket012  label="slideTableUpperMountHoleCaptiveNutL"
  BaseFeature = -> Pocket011
  Direction = (1,1e-16,1e-15)
  Length = 5
  Length2 = 5
  Placement = pos=(0,0,0) rot=(1,1,1;2.0944rad)
  Profile = -> Sketch034
  ReferenceAxis = -> Sketch034 [N_Axis]
  Refine = true
  Reversed = true
  Suppressed = false
  Type = 0
FEATURE [PartDesign::Mirrored] Mirrored003
  MirrorPlane = -> Sketch034 [V_Axis]
  Placement = pos=(0,0,0) rot=(1,1,1;2.0944rad)
  Refine = true
  Suppressed = false
  TransformMode = 0
FEATURE [PartDesign::LinearPattern] LinearPattern002
  Direction = -> Sketch034 [V_Axis]
  Length = 17
  Mode = 0
  Occurrences = 2
  Offset = 17
  Placement = pos=(0,0,0) rot=(1,1,1;2.0944rad)
  Refine = true
  Suppressed = false
  TransformMode = 0
FEATURE [PartDesign::LinearPattern] LinearPattern
  Direction = -> Sketch034 [V_Axis]
  Length = 17
  Mode = 0
  Occurrences = 2
  Offset = 17
  Placement = pos=(0,0,0) rot=(1,1,1;2.0944rad)
  Refine = true
  Reversed = true
  Suppressed = false
  TransformMode = 0
FEATURE [PartDesign::LinearPattern] LinearPattern003
  Direction = -> Sketch034 [V_Axis]
  Length = 17
  Mode = 0
  Occurrences = 2
  Offset = 17
  Placement = pos=(0,0,0) rot=(1,1,1;2.0944rad)
  Refine = true
  Suppressed = false
  TransformMode = 0
FEATURE [PartDesign::Mirrored] Mirrored004
  MirrorPlane = -> Sketch034 [V_Axis]
  Placement = pos=(0,0,0) rot=(1,1,1;2.0944rad)
  Refine = true
  Suppressed = false
  TransformMode = 0
FEATURE [Sketcher::SketchObject] Sketch035
  ArcFitTolerance = 1e-06
  AttachmentSupport = -> [XY_Plane004]
  FullyConstrained = true
  MakeInternals = false
  MapMode = 5
  sketch-geometry (6):
    g0: LineSegment StartX=-7.5 StartY=-57 StartZ=0 EndX=19 EndY=-57 EndZ=0
    g1: LineSegment StartX=19 StartY=-57 StartZ=0 EndX=19 EndY=-51 EndZ=0
    g2: LineSegment StartX=19 StartY=-51 StartZ=0 EndX=24.5 EndY=-51 EndZ=0
    g3: LineSegment StartX=24.5 StartY=-51 StartZ=0 EndX=24.5 EndY=-63 EndZ=0
    g4: LineSegment StartX=24.5 StartY=-63 StartZ=0 EndX=-7.5 EndY=-63 EndZ=0
    g5: LineSegment StartX=-7.5 StartY=-63 StartZ=0 EndX=-7.5 EndY=-57 EndZ=0
  constraints (18):
    c: Horizontal(g0)
    c: Coincident(g0,g1)
    c: Vertical(g1)
    c: Coincident(g1,g2)
    c: Horizontal(g2)
    c: Coincident(g2,g3)
    c: Vertical(g3)
    c: Coincident(g3,g4)
    c: Horizontal(g4)
    c: Coincident(g4,g5)
    c: Coincident(g5,g0)
    c: Parallel(g-2,g5)
    c: DistanceY(g1,g1) = 6
    c: DistanceX(g2,g2) = 5.5
    c: DistanceY(g5,g5) = 6
    c: DistanceX(g4,g-1) = 7.5
    c: DistanceX(g4,g4) = 32
    c: DistanceY(g0,g-1) = 57
FEATURE [PartDesign::Pad] Pad011  label="Base001"
  Direction = (0,0,1)
  Length = 4
  Length2 = 10
  Profile = -> Sketch035
  ReferenceAxis = -> Sketch035 [N_Axis]
  Refine = true
  Suppressed = false
  Type = 0
FEATURE [Sketcher::SketchObject] Sketch036
  ArcFitTolerance = 1e-06
  AttachmentSupport = -> [Pad011]
  ExternalGeometry = -> [Pad011]
  FullyConstrained = true
  MakeInternals = false
  MapMode = 5
  Placement = pos=(0,0,0) rot=(1,0,0;3.14159rad)
  sketch-geometry (6):
    g0: LineSegment StartX=-7.5 StartY=63 StartZ=0 EndX=24.5 EndY=63 EndZ=0
    g1: LineSegment StartX=24.5 StartY=63 StartZ=0 EndX=24.5 EndY=51 EndZ=0
    g2: LineSegment StartX=24.5 StartY=51 StartZ=0 EndX=17 EndY=51 EndZ=0
    g3: LineSegment StartX=17 StartY=51 StartZ=0 EndX=17 EndY=55 EndZ=0
    g4: LineSegment StartX=17 StartY=55 StartZ=0 EndX=-7.5 EndY=55 EndZ=0
    g5: LineSegment StartX=-7.5 StartY=55 StartZ=0 EndX=-7.5 EndY=63 EndZ=0
  constraints (15):
    c: Coincident(g-3,g0)
    c: Coincident(g0,g-4)
    c: Coincident(g0,g1)
    c: Coincident(g1,g-5)
    c: Coincident(g1,g2)
    c: Horizontal(g2)
    c: Coincident(g2,g3)
    c: Vertical(g3)
    c: Coincident(g3,g4)
    c: Horizontal(g4)
    c: Coincident(g4,g5)
    c: Coincident(g5,g0)
    c: Vertical(g5)
    c: DistanceY(g4,g-6) = 2
    c: DistanceX(g2,g-5) = 2
FEATURE [PartDesign::Pad] Pad012  label="Overhang"
  BaseFeature = -> Pad011
  Direction = (0,0,-1)
  Length = 4
  Length2 = 10
  Profile = -> Sketch036
  ReferenceAxis = -> Sketch036 [N_Axis]
  Refine = true
  Suppressed = false
  Type = 0
FEATURE [PartDesign::Pad] Pad013  label="YExtension"
  BaseFeature = -> Pad012
  Direction = (1,0,0)
  Length = 20
  Length2 = 10
  Profile = -> Pad012 [Face11]
  Refine = true
  Suppressed = false
  Type = 0
FEATURE [PartDesign::Pad] Pad014  label="ZExtension"
  BaseFeature = -> Pad013
  Direction = (0,1,0)
  Length = 10
  Length2 = 10
  Profile = -> Pad013 [Face11]
  Refine = true
  Suppressed = false
  Type = 0
FEATURE [Sketcher::SketchObject] Sketch037
  ArcFitTolerance = 1e-06
  AttachmentSupport = -> [Pad014]
  ExternalGeometry = -> [Pad014]
  FullyConstrained = true
  MakeInternals = false
  MapMode = 5
  Placement = pos=(0,0,-4) rot=(1,0,0;3.14159rad)
  sketch-geometry (4):
    g0: LineSegment StartX=-5.5 StartY=55 StartZ=0 EndX=6.5 EndY=55 EndZ=0
    g1: LineSegment StartX=6.5 StartY=55 StartZ=0 EndX=6.5 EndY=57 EndZ=0
    g2: LineSegment StartX=6.5 StartY=57 StartZ=0 EndX=-5.5 EndY=57 EndZ=0
    g3: LineSegment StartX=-5.5 StartY=57 StartZ=0 EndX=-5.5 EndY=55 EndZ=0
  constraints (12):
    c: Coincident(g0,g1)
    c: Coincident(g1,g2)
    c: Coincident(g2,g3)
    c: Coincident(g3,g0)
    c: Horizontal(g0)
    c: Horizontal(g2)
    c: Vertical(g1)
    c: Vertical(g3)
    c: Distance(g1,g3) = 12
    c: PointOnObject(g0,g-3)
    c: DistanceY(g-4,g2) = 0
    c: DistanceX(g-4,g2) = 2
FEATURE [PartDesign::Pocket] Pocket014  label="SlotForCamp"
  BaseFeature = -> Pad014
  Direction = (0,0,1)
  Length = 5
  Length2 = 5
  Profile = -> Sketch037
  ReferenceAxis = -> Sketch037 [N_Axis]
  Refine = true
  Suppressed = false
  Type = 0
FEATURE [Sketcher::SketchObject] Sketch038
  ArcFitTolerance = 1e-06
  AttachmentSupport = -> [Pocket014]
  ExternalGeometry = -> [Pocket014]
  FullyConstrained = true
  MakeInternals = false
  MapMode = 5
  Placement = pos=(0,-41,0) rot=(0,0.707107,0.707107;3.14159rad)
  sketch-geometry (4):
    g0: LineSegment StartX=-43.5 StartY=3 StartZ=0 EndX=-43.5 EndY=-2.9 EndZ=0
    g1: LineSegment StartX=-43.5 StartY=-2.9 StartZ=0 EndX=-30.6 EndY=-2.9 EndZ=0
    g2: LineSegment StartX=-30.6 StartY=-2.9 StartZ=0 EndX=-30.6 EndY=3 EndZ=0
    g3: LineSegment StartX=-30.6 StartY=3 StartZ=0 EndX=-43.5 EndY=3 EndZ=0
  constraints (12):
    c: Coincident(g0,g1)
    c: Coincident(g1,g2)
    c: Coincident(g2,g3)
    c: Coincident(g3,g0)
    c: Vertical(g0)
    c: Vertical(g2)
    c: Horizontal(g1)
    c: Horizontal(g3)
    c: Distance(g0,g2) = 12.9
    c: Distance(g1,g3) = 5.9
    c: DistanceX(g-4,g0) = 1
    c: DistanceY(g0,g-4) = 1
FEATURE [PartDesign::Pocket] Pocket015  label="SlotForSwitch"
  BaseFeature = -> Pocket014
  Direction = (0,-1,2e-16)
  Length = 5.9
  Length2 = 5
  Profile = -> Sketch038
  ReferenceAxis = -> Sketch038 [N_Axis]
  Refine = true
  Suppressed = false
  Type = 0
FEATURE [Sketcher::SketchObject] Sketch039
  ArcFitTolerance = 1e-06
  AttachmentSupport = -> [Pocket015]
  ExternalGeometry = -> [Pocket015]
  FullyConstrained = true
  MakeInternals = false
  MapMode = 5
  Placement = pos=(0,-46.9,0) rot=(0,0.707107,0.707107;3.14159rad)
  sketch-geometry (3):
    g0: Circle CenterX=-42.2 CenterY=0 CenterZ=0 NormalX=0 NormalY=0 NormalZ=1 AngleXU=0 Radius=1.5
    g1: Circle CenterX=-37.05 CenterY=0.05 CenterZ=0 NormalX=0 NormalY=0 NormalZ=1 AngleXU=0 Radius=1.5
    g2: Circle CenterX=-31.9 CenterY=0 CenterZ=0 NormalX=0 NormalY=0 NormalZ=1 AngleXU=0 Radius=1.5
  constraints (8):
    c: PointOnObject(g0,g-1)
    c: PointOnObject(g2,g-1)
    c: Equal(g2,g1)
    c: Equal(g1,g0)
    c: DistanceX(g0,g1) = 5.15
    c: DistanceX(g1,g2) = 5.15
    c: Symmetric(g-4,g-3,g1)
    c: Diameter(g1) = 3
FEATURE [PartDesign::Pocket] Pocket016  label="holesForWires"
  BaseFeature = -> Pocket015
  Direction = (0,-1,2e-16)
  Length = 20
  Length2 = 5
  Profile = -> Sketch039
  ReferenceAxis = -> Sketch039 [N_Axis]
  Refine = true
  Suppressed = false
  Type = 0
FEATURE [Sketcher::SketchObject] Sketch040
  ArcFitTolerance = 1e-06
  AttachmentSupport = -> [Pocket016]
  ExternalGeometry = -> [Pocket016]
  FullyConstrained = true
  MakeInternals = false
  MapMode = 5
  Placement = pos=(0,0,-4) rot=(1,0,0;3.14159rad)
  sketch-geometry (4):
    g0: Circle CenterX=40.3 CenterY=46.1 CenterZ=0 NormalX=0 NormalY=0 NormalZ=1 AngleXU=0 Radius=1.025
    g1: Circle CenterX=33.8 CenterY=46.1 CenterZ=0 NormalX=0 NormalY=0 NormalZ=1 AngleXU=0 Radius=1.025
    g2: LineSegment [constr] StartX=40.3 StartY=46.1 StartZ=0 EndX=33.8 EndY=46.1 EndZ=0
    g3: LineSegment [constr] StartX=40.3 StartY=46.1 StartZ=0 EndX=33.8 EndY=46.1 EndZ=0
  constraints (10):
    c: Equal(g1,g0)
    c: Diameter(g0) = 2.05
    c: DistanceX(g1,g0) = 6.5
    c: DistanceY(g-4,g1) = 5.1
    c: DistanceY(g0,g1) = 0
    c: Coincident(g2,g0)
    c: Coincident(g2,g1)
    c: Coincident(g3,g0)
    c: Coincident(g3,g1)
    c: DistanceX(g-4,g1) = 3.2
FEATURE [PartDesign::Pocket] Pocket017  label="holesForSwitch"
  BaseFeature = -> Pocket016
  Direction = (0,0,1)
  Length = 5
  Length2 = 5
  Profile = -> Sketch040
  ReferenceAxis = -> Sketch040 [N_Axis]
  Refine = true
  Suppressed = false
  Type = 0
FEATURE [Sketcher::SketchObject] Sketch041
  ArcFitTolerance = 1e-06
  AttachmentSupport = -> [Pocket017]
  ExternalGeometry = -> [Pocket017]
  FullyConstrained = true
  MakeInternals = false
  MapMode = 5
  Placement = pos=(0,-63,0) rot=(1,0,0;1.5708rad)
  sketch-geometry (2):
    g0: Circle CenterX=0.5 CenterY=2.025 CenterZ=0 NormalX=0 NormalY=0 NormalZ=1 AngleXU=0 Radius=1.025
    g1: Circle CenterX=8.5 CenterY=2.025 CenterZ=0 NormalX=0 NormalY=0 NormalZ=1 AngleXU=0 Radius=1.025
  constraints (6):
    c: Equal(g1,g0)
    c: Diameter(g0) = 2.05
    c: DistanceY(g0,g1) = 0
    c: DistanceY(g0,g-3) = 1.975
    c: DistanceX(g-4,g0) = 8
    c: DistanceX(g0,g1) = 8
FEATURE [PartDesign::Pocket] Pocket018
  BaseFeature = -> Pocket017
  Direction = (0,1,-2e-16)
  Length = 20
  Length2 = 5
  Profile = -> Sketch041
  ReferenceAxis = -> Sketch041 [N_Axis]
  Refine = true
  Suppressed = false
  Type = 0
FEATURE [Sketcher::SketchObject] Sketch042
  ArcFitTolerance = 1e-06
  AttachmentSupport = -> [Pocket012]
  ExternalGeometry = -> [Pocket012]
  FullyConstrained = true
  MakeInternals = false
  MapMode = 5
  Placement = pos=(1.3e-14,-1.38e-14,-20) rot=(0.707107,0.707107,0;3.14159rad)
  sketch-geometry (2):
    g0: Circle CenterX=-31.5 CenterY=-12.5 CenterZ=0 NormalX=0 NormalY=0 NormalZ=1 AngleXU=0 Radius=1.6
    g1: Circle CenterX=-51.5 CenterY=-12.5 CenterZ=0 NormalX=0 NormalY=0 NormalZ=1 AngleXU=0 Radius=1.6
  constraints (6):
    c: Equal(g0,g1)
    c: Diameter(g0) = 3.2
    c: DistanceY(g0,g1) = 0
    c: DistanceX(g1,g0) = 20
    c: DistanceY(g-4,g0) = 12.5
    c: DistanceX(g0,g-4) = 10
FEATURE [PartDesign::Pocket] Pocket019  label="clampMountHoles"
  BaseFeature = -> Pocket012
  Direction = (-1.8e-15,1.1e-15,1)
  Length = 5
  Length2 = 5
  Placement = pos=(0,0,0) rot=(1,1,1;2.0944rad)
  Profile = -> Sketch042
  ReferenceAxis = -> Sketch042 [N_Axis]
  Refine = true
  Suppressed = false
  Type = 0
FEATURE [PartDesign::Mirrored] Mirrored005
  BaseFeature = -> Pocket019
  MirrorPlane = -> XY_Plane
  Originals = -> [Pocket019]
  Placement = pos=(0,0,0) rot=(1,1,1;2.0944rad)
  Refine = true
  Suppressed = false
  TransformMode = 0
FEATURE [Sketcher::SketchObject] Sketch043
  ArcFitTolerance = 1e-06
  AttachmentSupport = -> [Mirrored005]
  ExternalGeometry = -> [Mirrored005]
  FullyConstrained = true
  MakeInternals = false
  MapMode = 5
  Placement = pos=(-4.7e-15,-21.5,0) rot=(0.57735,0.57735,0.57735;4.18879rad)
  sketch-geometry (2):
    g0: Circle CenterX=-18 CenterY=-12.5 CenterZ=0 NormalX=0 NormalY=0 NormalZ=1 AngleXU=0 Radius=1.025
    g1: Circle CenterX=-18 CenterY=-4.5 CenterZ=0 NormalX=0 NormalY=0 NormalZ=1 AngleXU=0 Radius=1.025
  constraints (6):
    c: Diameter(g0) = 2.05
    c: Equal(g1,g0)
    c: DistanceY(g0,g1) = 8
    c: DistanceX(g-4,g0) = 2
    c: DistanceY(g-4,g0) = 12.5
    c: DistanceX(g0,g1) = 0
FEATURE [PartDesign::Pocket] Pocket020
  BaseFeature = -> Mirrored005
  Direction = (1e-16,-1,2.3e-15)
  Length = 5
  Length2 = 5
  Placement = pos=(0,0,0) rot=(1,1,1;2.0944rad)
  Profile = -> Sketch043
  ReferenceAxis = -> Sketch043 [N_Axis]
  Refine = true
  Suppressed = false
  Type = 0
FEATURE [PartDesign::LinearPattern] LinearPattern004
  BaseFeature = -> Pocket020
  Direction = -> Y_Axis
  Length = 32
  Mode = 1
  Occurrences = 2
  Offset = 32
  Originals = -> [Pocket020]
  Placement = pos=(0,0,0) rot=(1,1,1;2.0944rad)
  Refine = true
  Reversed = true
  Suppressed = false
  TransformMode = 0
FEATURE [Sketcher::SketchObject] Sketch044
  ArcFitTolerance = 1e-06
  AttachmentSupport = -> [LinearPattern004]
  ExternalGeometry = -> [LinearPattern004]
  FullyConstrained = true
  MakeInternals = false
  MapMode = 5
  Placement = pos=(2,0,3.5e-15) rot=(0.57735,0.57735,-0.57735;4.18879rad)
  sketch-geometry (4):
    g0: LineSegment StartX=-53.5 StartY=16 StartZ=0 EndX=-57.5 EndY=16 EndZ=0
    g1: LineSegment StartX=-57.5 StartY=16 StartZ=0 EndX=-57.5 EndY=-16 EndZ=0
    g2: LineSegment StartX=-57.5 StartY=-16 StartZ=0 EndX=-53.5 EndY=-16 EndZ=0
    g3: LineSegment StartX=-53.5 StartY=-16 StartZ=0 EndX=-53.5 EndY=16 EndZ=0
  constraints (11):
    c: Coincident(g0,g1)
    c: Coincident(g1,g2)
    c: Coincident(g2,g3)
    c: Coincident(g3,g0)
    c: Horizontal(g0)
    c: Horizontal(g2)
    c: Vertical(g1)
    c: Vertical(g3)
    c: Distance(g1,g3) = 4
    c: PointOnObject(g0,g-3)
    c: Coincident(g1,g-4)
FEATURE [PartDesign::Pad] Pad015  label="topBrace"
  BaseFeature = -> LinearPattern004
  Direction = (-1,-1e-16,-1.9e-15)
  Length = 27
  Length2 = 10
  Placement = pos=(0,0,0) rot=(1,1,1;2.0944rad)
  Profile = -> Sketch044
  ReferenceAxis = -> Sketch044 [N_Axis]
  Refine = true
  Suppressed = false
  Type = 0
FEATURE [Sketcher::SketchObject] Sketch045
  ArcFitTolerance = 1e-06
  AttachmentSupport = -> [Pad015]
  FullyConstrained = false
  MakeInternals = false
  MapMode = 5
  Placement = pos=(-1.696e-13,-57.5,2.36e-14) rot=(0.57735,0.57735,-0.57735;2.0944rad)
  sketch-geometry (11):
    g0: LineSegment [constr] StartX=1.479e-13 StartY=2 StartZ=0 EndX=5.2e-15 EndY=-25 EndZ=0
    g1: GeomPoint [constr] X=7.65e-14 Y=-11.5 Z=0
    g2: Circle CenterX=7.65e-14 CenterY=-11.5 CenterZ=0 NormalX=0 NormalY=0 NormalZ=1 AngleXU=0 Radius=6
    g3: Circle CenterX=-9 CenterY=-2.5 CenterZ=0 NormalX=0 NormalY=0 NormalZ=1 AngleXU=0 Radius=2.1
    g4: Circle CenterX=9 CenterY=-2.5 CenterZ=0 NormalX=0 NormalY=0 NormalZ=1 AngleXU=0 Radius=2.1
    g5: Circle CenterX=9 CenterY=-20.5 CenterZ=0 NormalX=0 NormalY=0 NormalZ=1 AngleXU=0 Radius=2.1
    g6: Circle CenterX=-9 CenterY=-20.5 CenterZ=0 NormalX=0 NormalY=0 NormalZ=1 AngleXU=0 Radius=2.1
    g7: LineSegment [constr] StartX=-9 StartY=-2.5 StartZ=0 EndX=-9 EndY=-20.5 EndZ=0
    g8: LineSegment [constr] StartX=-9 StartY=-20.5 StartZ=0 EndX=9 EndY=-20.5 EndZ=0
    g9: LineSegment [constr] StartX=9 StartY=-20.5 StartZ=0 EndX=9 EndY=-2.5 EndZ=0
    g10: LineSegment [constr] StartX=9 StartY=-2.5 StartZ=0 EndX=-9 EndY=-2.5 EndZ=0
  constraints (21):
    c: Symmetric(g0,g0,g1)
    c: Diameter(g2) = 12
    c: Coincident(g2,g1)
    c: Equal(g6,g3)
    c: Equal(g6,g4)
    c: Equal(g6,g5)
    c: Diameter(g6) = 4.2
    c: Coincident(g7,g8)
    c: Coincident(g8,g9)
    c: Coincident(g9,g10)
    c: Coincident(g10,g7)
    c: Vertical(g7)
    c: Horizontal(g8)
    c: Coincident(g7,g3)
    c: Coincident(g8,g5)
    c: Coincident(g9,g4)
    c: Coincident(g6,g7)
    c: Symmetric(g5,g3,g1)
    c: Symmetric(g6,g4,g1)
    c: DistanceX(g10,g10) = 18
    c: Equal(g9,g10)
FEATURE [PartDesign::Pocket] Pocket021  label="wireHolesInTopBrance"
  BaseFeature = -> Pad015
  Direction = (2.8e-15,1,-1e-16)
  Length = 5
  Length2 = 5
  Placement = pos=(0,0,0) rot=(1,1,1;2.0944rad)
  Profile = -> Sketch045
  ReferenceAxis = -> Sketch045 [N_Axis]
  Refine = true
  Suppressed = false
  Type = 0
FEATURE [PartDesign::Fillet] Fillet001
  Base = -> Pocket021 [Edge113,Edge66,Edge39,Edge40,Edge37,Edge68,Edge100,Edge56,Edge69,Edge15,Edge55,Edge51,Edge38,Edge36,Edge33,Edge71,Edge118,Edge34,Edge59,Edge58,Edge46,Edge11,Edge63,Edge50,Edge53,Edge10,Edge52]
  BaseFeature = -> Pocket021
  Placement = pos=(0,0,0) rot=(1,1,1;2.0944rad)
  Radius = 1
  Refine = true
  SupportTransform = false
  Suppressed = false
  UseAllEdges = false
FEATURE [PartDesign::MultiTransform] MultiTransform  label="slideTableUpperMountHoleCaptiveNut"
  BaseFeature = -> Fillet001
  Originals = -> [Pocket012]
  Placement = pos=(0,0,0) rot=(1,1,1;2.0944rad)
  Refine = true
  Suppressed = false
  TransformMode = 0
  Transformations = -> [LinearPattern002,Mirrored003]
FEATURE [PartDesign::Pocket] Pocket013  label="slideTableUpperMountHoleCaptiveNutInsetL"
  BaseFeature = -> MultiTransform
  Direction = (1,1e-16,1e-15)
  Length = 1
  Length2 = 5
  Placement = pos=(0,0,0) rot=(1,1,1;2.0944rad)
  Profile = -> Sketch034
  ReferenceAxis = -> Sketch034 [N_Axis]
  Refine = true
  Suppressed = false
  Type = 0
FEATURE [PartDesign::MultiTransform] MultiTransform001  label="slideTableMountHoleCaptiveNut001"
  BaseFeature = -> Pocket013
  Originals = -> [Pocket013]
  Placement = pos=(0,0,0) rot=(1,1,1;2.0944rad)
  Refine = true
  Suppressed = false
  TransformMode = 0
  Transformations = -> [LinearPattern]
FEATURE [PartDesign::MultiTransform] MultiTransform002  label="slideTableMountHoleCaptiveNutInset"
  BaseFeature = -> MultiTransform001
  Originals = -> [Pocket013]
  Placement = pos=(0,0,0) rot=(1,1,1;2.0944rad)
  Refine = true
  Suppressed = false
  TransformMode = 0
  Transformations = -> [LinearPattern003,Mirrored004]
FEATURE [PartDesign::Body] Body  label="x_carriage"
  AllowCompound = false
  Group = -> [Sketch,Pad,Sketch002,Pad001,Sketch030,Pad009,Sketch031,Pocket009,Mirrored,Pad010,Sketch032,Pocket010,Mirrored001,Sketch033,Pocket011,Sketch034,Pocket012,Mirrored003,LinearPattern002,LinearPattern,LinearPattern003,Mirrored004,Sketch042,Pocket019,Mirrored005,Sketch043,Pocket020,LinearPattern004,Sketch044,Pad015,Sketch045,Pocket021,Fillet001,MultiTransform,Pocket013,MultiTransform001,+1 more]
  Origin = -> Origin
  Placement = pos=(13,0,108) rot=(0,0,1;0rad)
  Tip = -> Fillet001
FEATURE [PartDesign::Fillet] Fillet002
  Base = -> Pocket018 [Edge33,Edge41,Edge39,Edge64,Edge35,Edge26,Edge8,Edge11,Edge15,Edge40]
  BaseFeature = -> Pocket018
  Radius = 1
  Refine = true
  SupportTransform = false
  Suppressed = false
  UseAllEdges = false
FEATURE [PartDesign::Body] Body002  label="ZlimitSwitchHolder"
  AllowCompound = false
  Group = -> [Sketch035,Pad011,Sketch036,Pad012,Pad013,Pad014,Sketch037,Pocket014,Sketch038,Pocket015,Sketch039,Pocket016,Sketch040,Pocket017,Sketch041,Pocket018,Fillet002]
  Origin = -> Origin004
  Placement = pos=(0,0,87.8927) rot=(0,0,1;0rad)
  Tip = -> Fillet002
FEATURE [Sketcher::SketchObject] Sketch046
  ArcFitTolerance = 1e-06
  AttachmentSupport = -> [XY_Plane005]
  FullyConstrained = false
  MakeInternals = false
  MapMode = 5
  sketch-geometry (20):
    g0: LineSegment StartX=10.1159 StartY=-9.86641 StartZ=0 EndX=10.1159 EndY=-4.76641 EndZ=0
    g1: LineSegment StartX=10.1159 StartY=-4.76641 StartZ=0 EndX=8.31587 EndY=-2.96641 EndZ=0
    g2: LineSegment StartX=8.31587 StartY=-2.96641 StartZ=0 EndX=8.31587 EndY=3.23359 EndZ=0
    g3: LineSegment StartX=8.31587 StartY=3.23359 StartZ=0 EndX=10.1159 EndY=5.03359 EndZ=0
    g4: LineSegment StartX=10.1159 StartY=5.03359 StartZ=0 EndX=10.1159 EndY=10.1336 EndZ=0
    g5: LineSegment StartX=10.1159 StartY=10.1336 StartZ=0 EndX=5.54587 EndY=10.1336 EndZ=0
    g6: LineSegment StartX=5.54587 StartY=10.1336 StartZ=0 EndX=5.54587 EndY=18.8809 EndZ=0
    g7: LineSegment StartX=5.54587 StartY=18.8809 StartZ=0 EndX=-5.41413 EndY=18.8792 EndZ=0
    g8: LineSegment StartX=-5.41413 StartY=18.8792 StartZ=0 EndX=-5.56413 EndY=10.1331 EndZ=0
    g9: LineSegment StartX=-5.56413 StartY=10.1331 StartZ=0 EndX=-10.1341 EndY=10.1331 EndZ=0
    g10: LineSegment StartX=-10.1341 StartY=10.1331 StartZ=0 EndX=-10.1341 EndY=5.03311 EndZ=0
    g11: LineSegment StartX=-10.1341 StartY=5.03311 StartZ=0 EndX=-8.33413 EndY=3.23311 EndZ=0
    g12: LineSegment StartX=-8.33413 StartY=3.23311 StartZ=0 EndX=-8.33413 EndY=-2.96689 EndZ=0
    g13: LineSegment StartX=-8.33413 StartY=-2.96689 StartZ=0 EndX=-10.1341 EndY=-4.76689 EndZ=0
    g14: LineSegment StartX=-10.1341 StartY=-4.76689 StartZ=0 EndX=-10.0641 EndY=-9.86641 EndZ=0
    g15: LineSegment StartX=-10.0641 StartY=-9.86641 StartZ=0 EndX=-12.7705 EndY=-9.86641 EndZ=0
    g16: LineSegment StartX=-12.7705 StartY=-9.86641 StartZ=0 EndX=-12.7705 EndY=31.8179 EndZ=0
    g17: LineSegment StartX=-12.7705 StartY=31.8179 StartZ=0 EndX=12.8222 EndY=31.8179 EndZ=0
    g18: LineSegment StartX=12.8222 StartY=31.8179 StartZ=0 EndX=12.8222 EndY=-9.86641 EndZ=0
    g19: LineSegment StartX=12.8222 StartY=-9.86641 StartZ=0 EndX=10.1159 EndY=-9.86641 EndZ=0
  constraints (57):
    c: Coincident(g0,g1)
    c: Coincident(g1,g2)
    c: Coincident(g2,g3)
    c: Coincident(g3,g4)
    c: Coincident(g4,g5)
    c: Coincident(g5,g6)
    c: Coincident(g6,g7)
    c: Coincident(g7,g8)
    c: Coincident(g8,g9)
    c: Coincident(g9,g10)
    c: Coincident(g10,g11)
    c: Coincident(g11,g12)
    c: Coincident(g12,g13)
    c: Coincident(g13,g14)
    c: Equal(g14,g0)
    c: Equal(g12,g2)
    c: Equal(g4,g10)
    c: Equal(g9,g5)
    c: Equal(g6,g8)
    c: Perpendicular(g3,g1)
    c: Perpendicular(g11,g13)
    c: Equal(g10,g14)
    c: Equal(g13,g11)
    c: Equal(g0,g14)
    c: DistanceY(g13,g13) = 1.8
    c: DistanceY(g11,g11) = 1.8
    c: DistanceY(g3,g3) = 1.8
    c: DistanceY(g1,g1) = 1.8
    c: DistanceY(g2,g2) = 6.2
    c: DistanceY(g10,g10) = 5.1
    c: DistanceX(g3,g3) = 1.8
    c: DistanceX(g12,g12) = 0
    c: DistanceX(g9,g9) = 4.57
    c: DistanceX(g7,g7) = 10.96
    c: Coincident(g14,g15)
    c: Horizontal(g15)
    c: Coincident(g15,g16)
    c: Vertical(g16)
    c: Coincident(g16,g17)
    c: Horizontal(g17)
    c: Coincident(g17,g18)
    c: Vertical(g18)
    c: Coincident(g18,g19)
    c: Coincident(g19,g0)
    c: Horizontal(g19)
    c: Equal(g19,g15)
    c: Equal(g16,g18)
    c: DistanceX(g9,g4) = 20.25
    c: Perpendicular(g10,g9)
    c: Perpendicular(g2,g5)
    c: Perpendicular(g12,g9)
    c: Perpendicular(g4,g5)
    c: DistanceX(g11,g2) = 16.65
    c: DistanceX(g14,g0) = 20.18
    c: Perpendicular(g5,g6)
    c: Perpendicular(g9,g8)
    c: Equal(g9,g7)
FEATURE [PartDesign::Pad] Pad016  label="Body"
  Direction = (0,0,1)
  Length = 6
  Length2 = 10
  Profile = -> Sketch046
  ReferenceAxis = -> Sketch046 [N_Axis]
  Refine = true
  Suppressed = false
  Type = 0
FEATURE [PartDesign::Fillet] Fillet003
  Base = -> Pad016 [Edge53]
  BaseFeature = -> Pad016
  Radius = 4
  Refine = true
  SupportTransform = false
  Suppressed = false
  UseAllEdges = false
FEATURE [PartDesign::Fillet] Fillet004
  Base = -> Fillet003 [Edge3]
  BaseFeature = -> Fillet003
  Radius = 10
  Refine = true
  SupportTransform = false
  Suppressed = false
  UseAllEdges = false
FEATURE [Sketcher::SketchObject] Sketch047
  ArcFitTolerance = 1e-06
  AttachmentSupport = -> [Fillet004]
  FullyConstrained = false
  MakeInternals = false
  MapMode = 5
  Placement = pos=(-12.7705,0,0) rot=(0.57735,-0.57735,-0.57735;2.0944rad)
  sketch-geometry (1):
    g0: Circle CenterX=0 CenterY=2.99548 CenterZ=0 NormalX=0 NormalY=0 NormalZ=1 AngleXU=0 Radius=1.6
  constraints (2):
    c: Diameter(g0) = 3.2
    c: PointOnObject(g0,g-2)
FEATURE [PartDesign::Pocket] Pocket022
  BaseFeature = -> Fillet004
  Direction = (1,0,0)
  Length = 40
  Length2 = 5
  Profile = -> Sketch047
  ReferenceAxis = -> Sketch047 [N_Axis]
  Refine = true
  Suppressed = false
  Type = 0
FEATURE [PartDesign::Body] Body003  label="XSwitchTrigger"
  AllowCompound = false
  Group = -> [Sketch046,Pad016,Fillet003,Fillet004,Sketch047,Pocket022]
  Origin = -> Origin005
  Tip = -> Pocket022
